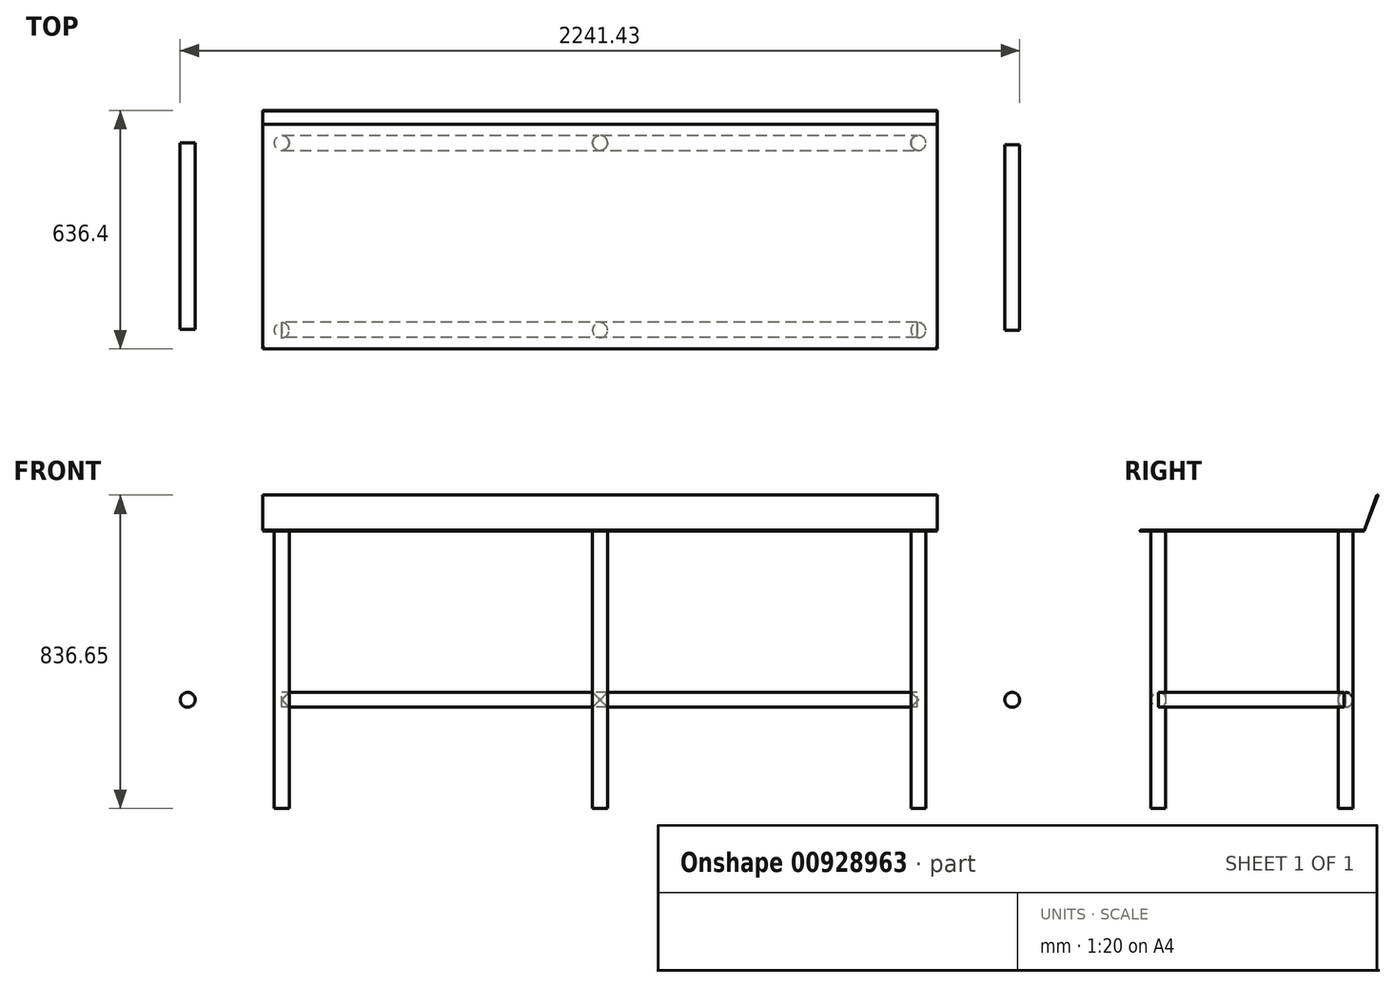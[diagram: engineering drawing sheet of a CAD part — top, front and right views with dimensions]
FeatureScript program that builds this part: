
annotation { "Feature Type Name" : "Feature", "Feature Type Description" : "" }
export const myFeature = defineFeature(function(context is Context, id is Id, definition is map)
    precondition{}
    {
        {
            var Q0;
            Q0=qCreatedBy(makeId("Top.planeOp"),FACE);
            var sketch = newSketch(context, id + "F0", { "sketchPlane" : qUnion([Q0])});
            skLineSegment(sketch, "E0", {"start": v(0, 1117.67) * mm, "end": v(0, -953.15) * mm, "construction": true});
            skLineSegment(sketch, "E1", {"start": v(-1368.46, 0) * mm, "end": v(1233.33, 0) * mm, "construction": true});
            skCircle(sketch, "E2", {"center": v(-850, 250) * mm, "radius": 20 * mm});
            skCircle(sketch, "E3", {"center": v(-850, -250) * mm, "radius": 20 * mm});
            skCircle(sketch, "E4", {"center": v(850, 250) * mm, "radius": 20 * mm});
            skCircle(sketch, "E5", {"center": v(850, -250) * mm, "radius": 20 * mm});
            skCircle(sketch, "E6", {"center": v(0, 250) * mm, "radius": 20 * mm});
            skCircle(sketch, "E7", {"center": v(0, -250) * mm, "radius": 20 * mm});
            skSolve(sketch);
        }
        {
            var Q0;
            Q0 = qSketchRegion(id + "F0", true);
            extrude(context, id + "F1", {"entities" : qUnion([Q0]), "depth" : 740 * mm, "offsetDistance" : 25.4 * mm});
        }
        {
            var Q0;
            Q0=makeQuery(id+"F1.opExtrude","CAP_FACE",FACE,{"disambiguationData":[OSD([sQuery(id+"F0.wireOp",EDGE,"E6")])],"isStart":false});
            var sketch = newSketch(context, id + "F2", { "sketchPlane" : qUnion([Q0])});
            skLineSegment(sketch, "E8", {"start": v(0, 526.99) * mm, "end": v(0, -382.73) * mm, "construction": true});
            skLineSegment(sketch, "E9", {"start": v(-914.77, 0) * mm, "end": v(904.67, 0) * mm, "construction": true});
            skLineSegment(sketch, "E10.bottom", {"start": v(-900, 300) * mm, "end": v(900, 300) * mm});
            skLineSegment(sketch, "E10.top", {"start": v(-900, -300) * mm, "end": v(900, -300) * mm});
            skLineSegment(sketch, "E10.left", {"start": v(-900, 300) * mm, "end": v(-900, -300) * mm});
            skLineSegment(sketch, "E10.right", {"start": v(900, 300) * mm, "end": v(900, -300) * mm});
            skSolve(sketch);
        }
        {
            var Q0;
            Q0 = qSketchRegion(id + "F2", true);
            extrude(context, id + "F3", {"entities" : qUnion([Q0]), "depth" : 3 * mm, "offsetDistance" : 25.4 * mm});
        }
        {
            var Q0;
            Q0=makeQuery(id+"F3.opExtrude","SWEPT_FACE",FACE,{"disambiguationData":[OSD([sQuery(id+"F2.wireOp",EDGE,"E10.left")])]});
            var sketch = newSketch(context, id + "F4", { "sketchPlane" : qUnion([Q0])});
            skLineSegment(sketch, "E11", {"start": v(-300, 743) * mm, "end": v(-333.52, 835.09) * mm});
            skLineSegment(sketch, "E12", {"start": v(-335.08, 836.65) * mm, "end": v(-336.08, 836.29) * mm});
            skPoint(sketch, "E13.visualSharp", {"position": v(-334.2, 836.97) * mm});
            skArc(sketch, "E13.filletArc", {"start": v(-333.52, 835.09) * mm, "mid": v(-334.55, 836.22) * mm, "end": v(-336.08, 836.29) * mm});
            skLineSegment(sketch, "E14", {"start": v(-336.26, 834.03) * mm, "end": v(-300, 743) * mm});
            skPoint(sketch, "E15.visualSharp", {"position": v(-337.02, 835.94) * mm});
            skArc(sketch, "E15.filletArc", {"start": v(-335.08, 836.65) * mm, "mid": v(-336.23, 835.59) * mm, "end": v(-336.26, 834.03) * mm});
            skSolve(sketch);
        }
        {
            var Q0;
            Q0 = qSketchRegion(id + "F4", true);
            var Q1;
            Q1=makeQuery(id+"F3.opExtrude","SWEPT_FACE",FACE,{"disambiguationData":[OSD([sQuery(id+"F2.wireOp",EDGE,"E10.right")])]});
            extrude(context, id + "F5", {"entities" : qUnion([Q0]), "endBound" : BoundingType.UP_TO_SURFACE, "oppositeDirection" : true, "depth" : 25.4 * mm, "endBoundEntityFace" : qUnion([Q1]), "offsetDistance" : 25.4 * mm});
        }
        {
            var Q0;
            Q0=makeQuery(id+"F3.opExtrude","CAP_EDGE",EDGE,{"disambiguationData":[OSD([sQuery(id+"F2.wireOp",EDGE,"E10.right")])],"isStart":false});
            var Q1;
            Q1=makeQuery(id+"F3.opExtrude","CAP_EDGE",EDGE,{"disambiguationData":[OSD([sQuery(id+"F2.wireOp",EDGE,"E10.top")])],"isStart":false});
            var Q2;
            Q2=makeQuery(id+"F3.opExtrude","CAP_EDGE",EDGE,{"disambiguationData":[OSD([sQuery(id+"F2.wireOp",EDGE,"E10.left")])],"isStart":false});
            fillet(context, id + "F6", {"entities" : qUnion([Q0, Q1, Q2]), "radius" : 5.08 * mm, "tangentPropagation" : true, "allowEdgeOverflow" : false});
        }
        {
            var Q0;
            Q0=makeQuery(id+"F1.opExtrude","CAP_EDGE",EDGE,{"disambiguationData":[OSD([sQuery(id+"F0.wireOp",EDGE,"E3")])],"isStart":true});
            cPlane(context, id + "F7", {"entities" : qUnion([Q0]), "cplaneType" : CPlaneType.LINE_ANGLE, "offset" : 25.4 * mm, "angle" : 0 * degree, "width" : 152.4 * mm, "height" : 152.4 * mm});
        }
        {
            var Q0;
            Q0=qCreatedBy(id+"F7.planeOp",FACE);
            var sketch = newSketch(context, id + "F8", { "sketchPlane" : qUnion([Q0])});
            skCircle(sketch, "E16", {"center": v(-249, 290) * mm, "radius": 20 * mm});
            skSolve(sketch);
        }
        {
            var Q0;
            Q0 = qSketchRegion(id + "F8", true);
            extrude(context, id + "F9", {"entities" : qUnion([Q0]), "depth" : 1696.72 * mm, "offsetDistance" : 25.4 * mm});
        }
        {
            var Q0;
            Q0=makeQuery(id+"F1.opExtrude","CAP_EDGE",EDGE,{"disambiguationData":[OSD([sQuery(id+"F0.wireOp",EDGE,"E5")])],"isStart":true});
            cPlane(context, id + "F10", {"entities" : qUnion([Q0]), "cplaneType" : CPlaneType.LINE_ANGLE, "offset" : 25.4 * mm, "angle" : 90 * degree, "width" : 152.4 * mm, "height" : 152.4 * mm});
        }
        {
            var Q0;
            Q0=qCreatedBy(id+"F10.planeOp",FACE);
            var sketch = newSketch(context, id + "F11", { "sketchPlane" : qUnion([Q0])});
            skCircle(sketch, "E17", {"center": v(-1100.47, 290) * mm, "radius": 20 * mm});
            skSolve(sketch);
        }
        {
            var Q0;
            Q0 = qSketchRegion(id + "F11", true);
            extrude(context, id + "F12", {"entities" : qUnion([Q0]), "depth" : 495.3 * mm, "offsetDistance" : 25.4 * mm});
        }
        {
            var Q0;
            Q0=makeQuery(id+"F1.opExtrude","CAP_EDGE",EDGE,{"disambiguationData":[OSD([sQuery(id+"F0.wireOp",EDGE,"E4")])],"isStart":true});
            cPlane(context, id + "F13", {"entities" : qUnion([Q0]), "cplaneType" : CPlaneType.LINE_ANGLE, "offset" : 25.4 * mm, "angle" : 0 * degree, "width" : 152.4 * mm, "height" : 152.4 * mm});
        }
        {
            var Q0;
            Q0=qCreatedBy(id+"F13.planeOp",FACE);
            var sketch = newSketch(context, id + "F14", { "sketchPlane" : qUnion([Q0])});
            skCircle(sketch, "E18", {"center": v(249.89, 290) * mm, "radius": 20 * mm});
            skSolve(sketch);
        }
        {
            var Q0;
            Q0 = qSketchRegion(id + "F14", true);
            extrude(context, id + "F15", {"entities" : qUnion([Q0]), "operationType" : NewBodyOperationType.ADD, "oppositeDirection" : true, "depth" : 1696.72 * mm, "offsetDistance" : 25.4 * mm});
        }
        {
            var Q0;
            Q0=makeQuery(id+"F1.opExtrude","CAP_EDGE",EDGE,{"disambiguationData":[OSD([sQuery(id+"F0.wireOp",EDGE,"E2")])],"isStart":true});
            cPlane(context, id + "F16", {"entities" : qUnion([Q0]), "cplaneType" : CPlaneType.LINE_ANGLE, "offset" : 25.4 * mm, "angle" : 90 * degree, "width" : 152.4 * mm, "height" : 152.4 * mm});
        }
        {
            var Q0;
            Q0=qCreatedBy(id+"F16.planeOp",FACE);
            var sketch = newSketch(context, id + "F17", { "sketchPlane" : qUnion([Q0])});
            skCircle(sketch, "E19", {"center": v(1100.96, 290) * mm, "radius": 20 * mm});
            skSolve(sketch);
        }
        {
            var Q0;
            Q0 = qSketchRegion(id + "F17", true);
            extrude(context, id + "F18", {"entities" : qUnion([Q0]), "operationType" : NewBodyOperationType.ADD, "oppositeDirection" : true, "depth" : 497.84 * mm, "offsetDistance" : 25.4 * mm});
        }
    });
